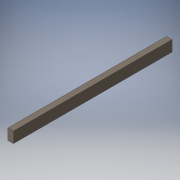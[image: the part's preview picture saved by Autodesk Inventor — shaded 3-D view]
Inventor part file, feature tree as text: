
AUTODESK INVENTOR PART (.ipt)
format: ipt  version: 2016 (Build 200138000, 138)  size: 93,696 bytes
history: native  units: in
note: dims shown in document units (in); Inventor stores cm internally (conversion verified against a paired STEP export)
features: extrude x1, sketch x1
ambient origin geometry x8: Origin, YZ Plane, XZ Plane, XY Plane, X Axis, Y Axis, Z Axis, Center Point
bodies: Solid1 (feature_tree)
feature tree (2):
  extrude  "Extrusion1"  Depth=4.0in
  sketch  "Sketch1"  dims[d0=2.0in d1=4.0in d2=58.0in d3=0.0in]
